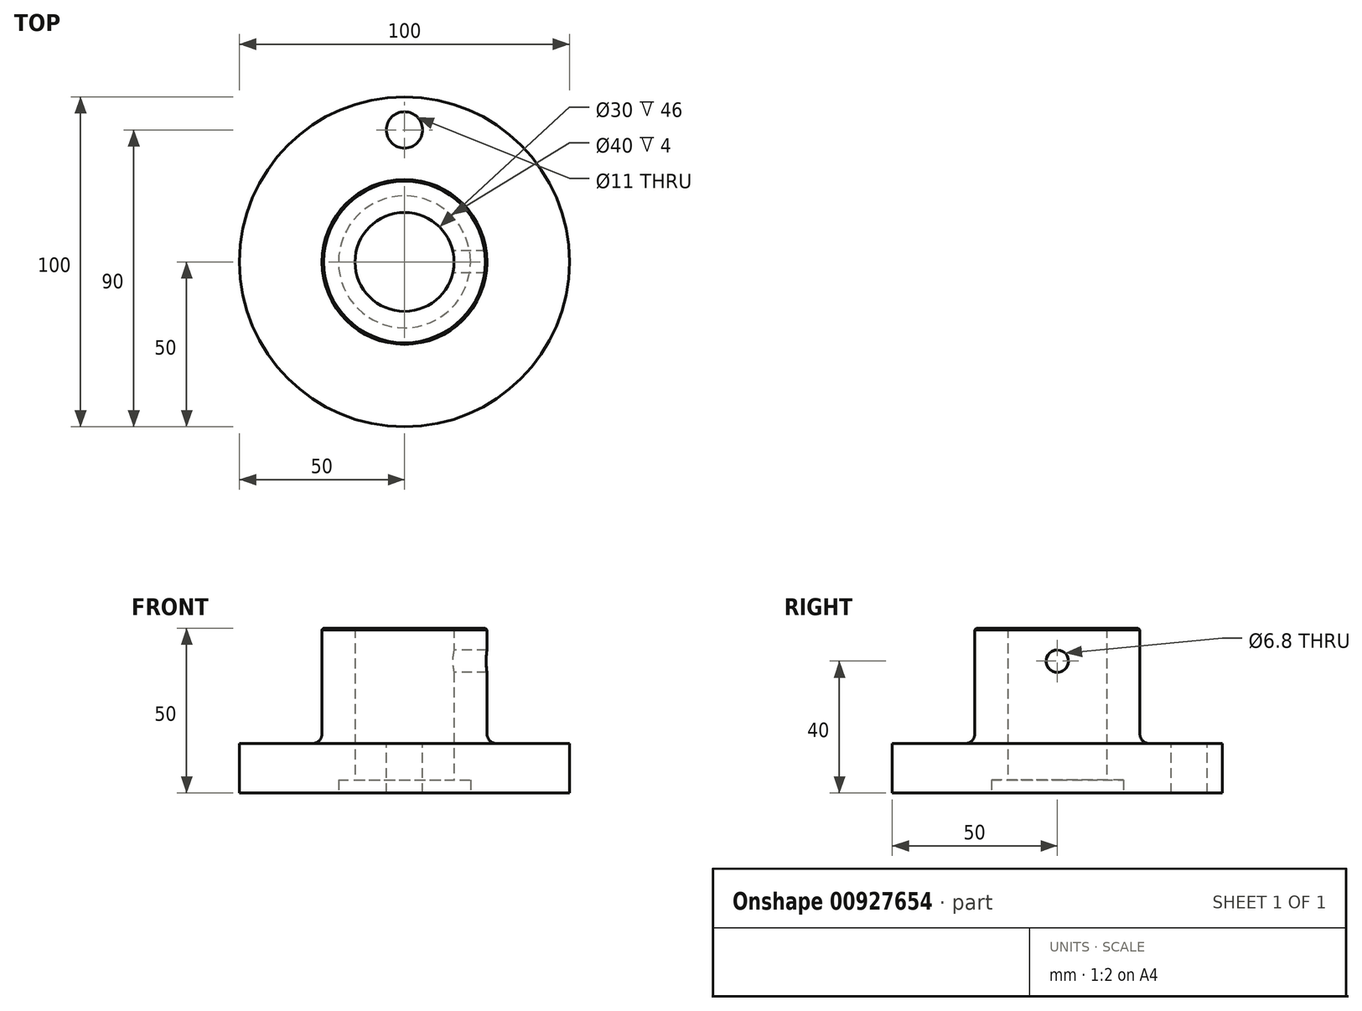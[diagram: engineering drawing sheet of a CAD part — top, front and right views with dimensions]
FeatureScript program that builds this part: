
annotation { "Feature Type Name" : "Feature", "Feature Type Description" : "" }
export const myFeature = defineFeature(function(context is Context, id is Id, definition is map)
    precondition{}
    {
        {
            var Q0;
            Q0=qCreatedBy(makeId("Front.planeOp"),FACE);
            var sketch = newSketch(context, id + "F0", { "sketchPlane" : qUnion([Q0])});
            skLineSegment(sketch, "E0", {"start": v(0, 0) * mm, "end": v(0, 67.45) * mm, "construction": true});
            skLineSegment(sketch, "E1", {"start": v(-15, 50) * mm, "end": v(-25, 50) * mm});
            skLineSegment(sketch, "E2", {"start": v(-25, 50) * mm, "end": v(-25, 15) * mm});
            skLineSegment(sketch, "E3", {"start": v(-25, 15) * mm, "end": v(-50, 15) * mm});
            skLineSegment(sketch, "E4", {"start": v(-50, 15) * mm, "end": v(-50, 0) * mm});
            skLineSegment(sketch, "E5", {"start": v(-50, 0) * mm, "end": v(-20, 0) * mm});
            skLineSegment(sketch, "E6", {"start": v(-20, 4) * mm, "end": v(-20, 0) * mm});
            skLineSegment(sketch, "E7", {"start": v(-20, 4) * mm, "end": v(-15, 4) * mm});
            skLineSegment(sketch, "E8", {"start": v(-15, 50) * mm, "end": v(-15, 4) * mm});
            skSolve(sketch);
        }
        {
            var Q0;
            Q0 = qSketchRegion(id + "F0", true);
            var Q1;
            Q1=sQuery(id+"F0.wireOp",EDGE,"E0");
            revolve(context, id + "F1", {"surfaceOperationType" : NewSurfaceOperationType.NEW, "entities" : qUnion([Q0]), "axis" : qUnion([Q1]), "revolveType" : RevolveType.FULL});
        }
        {
            var Q0;
            Q0=makeQuery(id+"F1.opRevolve","SWEPT_EDGE",EDGE,{"disambiguationData":[OSD([sQuery(id+"F0.wireOp",EDGE,"E2"),sQuery(id+"F0.wireOp",EDGE,"E3")])]});
            fillet(context, id + "F2", {"entities" : qUnion([Q0]), "radius" : 3 * mm, "tangentPropagation" : true, "allowEdgeOverflow" : false});
        }
        {
            var Q0;
            Q0=qCreatedBy(makeId("Right.planeOp"),FACE);
            var sketch = newSketch(context, id + "F3", { "sketchPlane" : qUnion([Q0])});
            skPoint(sketch, "E9", {"position": v(0, 40) * mm});
            skSolve(sketch);
        }
        {
            var Q0;
            Q0=sQuery(id+"F3.wireOp",VERTEX,"E9");
            var Q1;
            Q1=makeQuery(id+"F1.opRevolve","SWEPT_BODY",BODY,{"disambiguationData":[OSD([sQuery(id+"F0.wireOp",EDGE,"BUsvgQcl-KfWQ-WjHX-3a6k-cHchIgCphpCN"),sQuery(id+"F0.wireOp",EDGE,"E1"),sQuery(id+"F0.wireOp",EDGE,"E2"),sQuery(id+"F0.wireOp",EDGE,"E3"),sQuery(id+"F0.wireOp",EDGE,"E4"),sQuery(id+"F0.wireOp",EDGE,"E5"),sQuery(id+"F0.wireOp",EDGE,"E6"),sQuery(id+"F0.wireOp",EDGE,"E7")])]});
            hole(context, id + "F4", {"style" : HoleStyle.SIMPLE, "endStyle" : HoleEndStyle.THROUGH, "oppositeDirection" : true, "standardTappedOrClearance" : lookupTablePath({ "standard" : "ISO", "engagement" : "75%", "pitch" : "1.25 mm", "size" : "M8", "type" : "Tapped" }), "standardBlindInLast" : lookupTablePath({ "standard" : "ISO", "engagement" : "75%", "pitch" : "1.25 mm", "size" : "M8", "type" : "Tapped" }), "holeDiameter" : 6.8 * mm, "majorDiameter" : 8 * mm, "showTappedDepth" : true, "isTappedThrough" : true, "tappedDepth" : 12 * mm, "tapClearance" : 3, "locations" : qUnion([Q0]), "scope" : qUnion([Q1])});
        }
        {
            var Q0;
            Q0=makeQuery(id+"F1.opRevolve","SWEPT_FACE",FACE,{"disambiguationData":[OSD([sQuery(id+"F0.wireOp",EDGE,"E3")])]});
            var sketch = newSketch(context, id + "F5", { "sketchPlane" : qUnion([Q0])});
            skCircle(sketch, "E10", {"center": v(0, 0) * mm, "radius": 40 * mm, "construction": true});
            skCircle(sketch, "E11", {"center": v(0, 40) * mm, "radius": 5.5 * mm});
            skSolve(sketch);
        }
        {
            var Q0;
            Q0 = qSketchRegion(id + "F5", true);
            extrude(context, id + "F6", {"entities" : qUnion([Q0]), "operationType" : NewBodyOperationType.REMOVE, "endBound" : BoundingType.THROUGH_ALL, "oppositeDirection" : true, "depth" : 25 * mm, "offsetDistance" : 25 * mm});
        }
        {
            var Q0;
            Q0=makeQuery(id+"F1.opRevolve","SWEPT_EDGE",EDGE,{"disambiguationData":[OSD([sQuery(id+"F0.wireOp",EDGE,"E1"),sQuery(id+"F0.wireOp",EDGE,"E2")])]});
            chamfer(context, id + "F7", {"entities" : qUnion([Q0]), "width" : 0.5 * mm, "tangentPropagation" : true});
        }
    });
